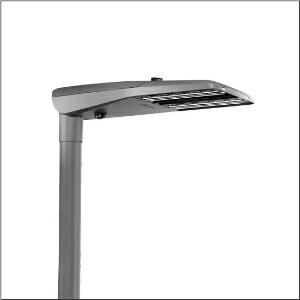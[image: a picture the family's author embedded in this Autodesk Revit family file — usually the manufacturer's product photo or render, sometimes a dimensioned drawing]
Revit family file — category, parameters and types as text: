
# Revit family: streetlight_sl_11_iq_midi___st1_0st0_5_5xc3j51y08me_1f9d
name_source: partatom
category: Lighting Fixtures
units: mm (PartAtom-declared; Revit-internal decimal feet)

## family parameters
Cut with Voids When Loaded = No
Host = Face
Light Source = No
Part Type = Normal
Room Calculation Point = No
Round Connector Dimension = Use Diameter
Shared = No

## types (1)
- --- (1 x LED, 17650 lm, 122.7 W, 3000K)
    Apparent Load = 123 VA
    CIE Flux Codes = 35 68 96 100 100
    Color Rendering = 70
    Color Temperature = 3000K
    Default Elevation = 1800 mm
    Description = Streetlight SL 11 iQ midi, mast luminaire, primary light control with 3 zone facetted reflector, of plastic, silver coated, highly specular, primary optical cover: cover, of PMMA, transparent, light distribution: ST1.0ST0.5, light emission: direct distribution, primary light characteristic: asymmetric, installation type: post-top, side-entry, LED, High Power LED, rated luminous flux: 17.650lm, luminous efficacy: 144lm/W, light colour: 730, colour temperature: 3000K, control: presetting dimming logarithmic, Street-Remote, Auto-Match, Temp-Guard, Lumen-Switch, Night-Set, Smart-Wire, Light-Fading, Desk-Remote (wireless, voltage-free reading and setting of iQ features in the workshop via application-optimized NFC function/RFID function), optimised constant luminous flux control (CLO 2.0), with cable H07RN-F 5x 1.5mm², mains connection: 230..240V, AC, 50/60Hz, connection cable pre-assembled, cable length: 12,5m, start of lifetime: 123W, end of service life: 130W, reduction: 56W, luminaire housing, of diecast aluminium, powder-coated, Siteco® metallic grey (DB 702S), please order mast flange separately, inclination adjustable without tools: 0°, 5°, 10°, 15° (post-top) | 0°, -5°, -10°, -15° (side-entry), sealing non-destructively replaceable, multi-level sealing system, length: 780mm, width: 376mm, height: 118mm, mast flange for spigot size: 42mm (side-entry): 5XC10008XM4, 60/48mm (side-entry/post-top): 5XC10108XM2, 76/60mm (side-entry/post-top): 5XC10108XM1, equipment: Power, Smart Interface below and above, protection rating (complete): IP66, insulation class (complete): insulation class II (safety insulation), certification: CE, ENEC, VDE, UKCA, impact resistance: IK09, permissible operating ambient temperature for outdoor applications: -25..+50°C, standard-compliant lighting for roads and squares, Environmental Product Declaration (EPD) tested and certified by an independent institute, packaging unit: 1 piece

Light Distribution: ST1.0ST0.5
    Height = 118 mm
    Lamp = 1 x LED
    Lamp Light Flux = 17650 lm
    Lamp Power = 122.7 W
    Lamp count = 1
    Length = 780 mm
    Luminous efficacy = 144 lm/W
    Manufacturer = Siteco
    ModVariant = No
    Model = 5XC3J51Y08ME
    Number of Poles = 1
    OnlyDefault = Yes
    Power Factor = 1
    Product Name = Streetlight SL 11 iQ midi | ST1.0ST0.5
    Product group = mast luminaire | pylon top
    ProductGroupID = 6100
    Protection Class = Protection class II
    Protection Degree = IP 66
    RLX_Detail_Level = 1
    RLX_Emergency_Light_Flux = 0 lm
    RLX_Emergency_Type = 0
    RLX_Emergency_Type_DB = No
    RlxData = <blob elided: 69565 chars, md5=db9ff63d>
    Socket = socket
    Standby Power = 0 W
    System Light Flux = 17650 lm
    System Power = 123 W
    Type Comments = factory setting: luminous flux: 100 % | dim-lin: 254 | 553 mA
    Type Image = l_1004429.jpg
    URL = http://relux.com
    VarID = @adj_002921
    Voltage = 0 V
    Weight = 0.00 kg
    Width = 376 mm

## geometry (parser evidence)
native form markers: Blend x4, Sweep x8
no freeform markers — native parametric forms only
